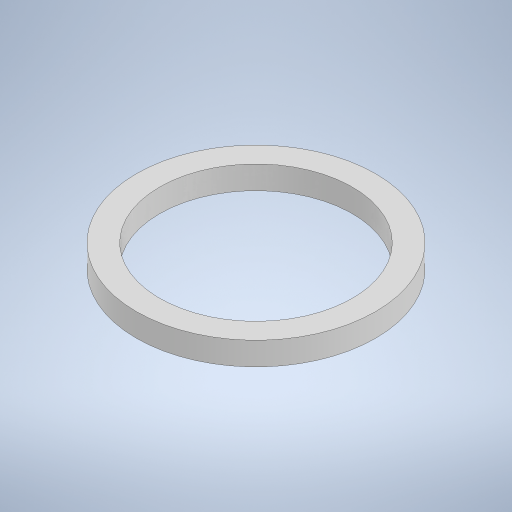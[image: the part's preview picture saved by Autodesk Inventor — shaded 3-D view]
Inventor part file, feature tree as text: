
AUTODESK INVENTOR PART (.ipt)
format: ipt  version: 2023 (Build 270158000, 158)  size: 230,400 bytes
history: native  units: in
note: dims shown in document units (in); Inventor stores cm internally (conversion verified against a paired STEP export)
features: extrude x1, sketch x1
ambient origin geometry x8: Origin, YZ Plane, XZ Plane, XY Plane, X Axis, Y Axis, Z Axis, Center Point
bodies: Solid1 (feature_tree)
feature tree (2):
  extrude  "Extrusion1"  Depth=0.2362in
  sketch  "Sketch1"  dims[d0=2.4409in d1=1.9685in d2=0.2362in d3=0.0in]
